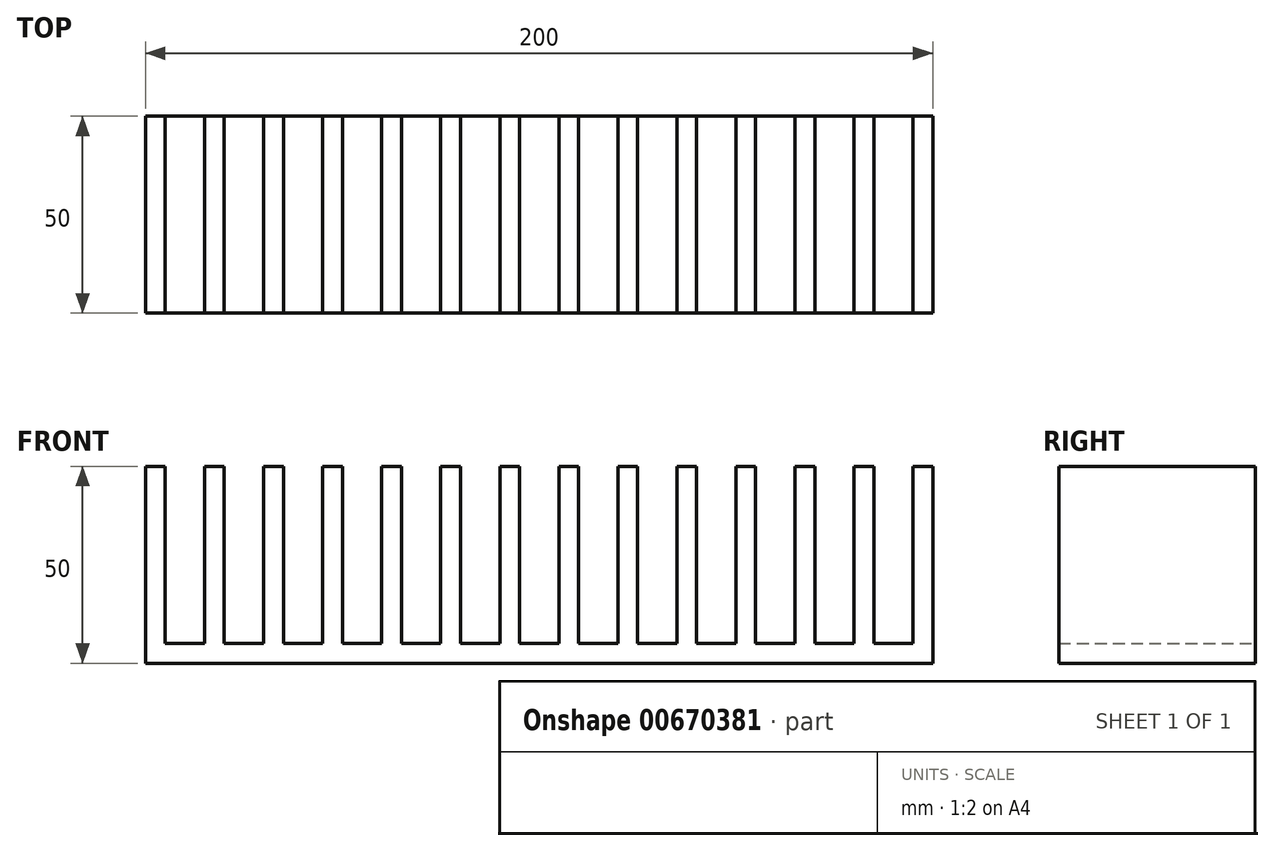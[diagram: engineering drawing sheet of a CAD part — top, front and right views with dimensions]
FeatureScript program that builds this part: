
annotation { "Feature Type Name" : "Feature", "Feature Type Description" : "" }
export const myFeature = defineFeature(function(context is Context, id is Id, definition is map)
    precondition{}
    {
        {
            var Q0;
            Q0=qCreatedBy(makeId("Top.planeOp"),FACE);
            var sketch = newSketch(context, id + "F0", { "sketchPlane" : qUnion([Q0])});
            skLineSegment(sketch, "E0.bottom", {"start": v(-104.93, 24.44) * mm, "end": v(95.07, 24.44) * mm});
            skLineSegment(sketch, "E0.top", {"start": v(-104.93, -25.56) * mm, "end": v(95.07, -25.56) * mm});
            skLineSegment(sketch, "E0.left", {"start": v(-104.93, 24.44) * mm, "end": v(-104.93, -25.56) * mm});
            skLineSegment(sketch, "E0.right", {"start": v(95.07, 24.44) * mm, "end": v(95.07, -25.56) * mm});
            skLineSegment(sketch, "E1", {"start": v(-99.93, 24.44) * mm, "end": v(-99.93, -25.56) * mm});
            skLineSegment(sketch, "E2", {"start": v(-89.93, -25.56) * mm, "end": v(-89.93, 24.44) * mm});
            skLineSegment(sketch, "E3", {"start": v(-84.93, 24.44) * mm, "end": v(-84.93, -25.56) * mm});
            skLineSegment(sketch, "E4", {"start": v(-74.93, -25.56) * mm, "end": v(-74.93, 24.44) * mm});
            skLineSegment(sketch, "E5", {"start": v(-69.93, 24.44) * mm, "end": v(-69.93, -25.56) * mm});
            skLineSegment(sketch, "E6", {"start": v(-59.93, -25.56) * mm, "end": v(-59.93, 24.44) * mm});
            skLineSegment(sketch, "E7", {"start": v(-54.93, 24.44) * mm, "end": v(-54.93, -25.56) * mm});
            skLineSegment(sketch, "E8", {"start": v(-44.93, -25.56) * mm, "end": v(-44.93, 24.44) * mm});
            skLineSegment(sketch, "E9", {"start": v(-39.93, 24.44) * mm, "end": v(-39.93, -25.56) * mm});
            skLineSegment(sketch, "E10", {"start": v(-29.93, -25.56) * mm, "end": v(-29.93, 24.44) * mm});
            skLineSegment(sketch, "E11", {"start": v(-24.93, 24.44) * mm, "end": v(-24.93, -25.56) * mm});
            skLineSegment(sketch, "E12", {"start": v(-14.93, 24.44) * mm, "end": v(-14.93, -25.56) * mm});
            skLineSegment(sketch, "E13", {"start": v(-9.93, -25.56) * mm, "end": v(-9.93, 24.44) * mm});
            skPoint(sketch, "E13.endSnap0", {"position": v(-4.93, 24.44) * mm});
            skLineSegment(sketch, "E14", {"start": v(5.07, 24.44) * mm, "end": v(5.07, -25.56) * mm});
            skLineSegment(sketch, "E15", {"start": v(0.07, -25.56) * mm, "end": v(0.07, 24.44) * mm});
            skLineSegment(sketch, "E16", {"start": v(15.07, 24.44) * mm, "end": v(15.07, -25.56) * mm});
            skLineSegment(sketch, "E17", {"start": v(20.07, -25.56) * mm, "end": v(20.07, 24.44) * mm});
            skLineSegment(sketch, "E18", {"start": v(35.07, 24.44) * mm, "end": v(35.07, -25.56) * mm});
            skLineSegment(sketch, "E19", {"start": v(30.07, -25.56) * mm, "end": v(30.07, 24.44) * mm});
            skLineSegment(sketch, "E20", {"start": v(45.07, -25.56) * mm, "end": v(45.07, 24.44) * mm});
            skLineSegment(sketch, "E21", {"start": v(50.07, 24.44) * mm, "end": v(50.07, -25.56) * mm});
            skLineSegment(sketch, "E22", {"start": v(60.07, 24.44) * mm, "end": v(60.07, -25.56) * mm});
            skLineSegment(sketch, "E23", {"start": v(65.07, -25.56) * mm, "end": v(65.07, 24.44) * mm});
            skLineSegment(sketch, "E24", {"start": v(75.07, 24.44) * mm, "end": v(75.07, -25.56) * mm});
            skLineSegment(sketch, "E25", {"start": v(80.07, -25.56) * mm, "end": v(80.07, 24.44) * mm});
            skLineSegment(sketch, "E26", {"start": v(90.07, 24.44) * mm, "end": v(90.07, -25.56) * mm});
            skSolve(sketch);
        }
        {
            var Q0;
            {var subQ0=sQuery(id+"F0.wireOp",EDGE,"E22");Q0=makeQuery(id+"F0.imprint","IMPRINT",FACE,{"disambiguationData":[TD([[makeQuery(id+"F0.imprint","IMPRINT",EDGE,{"derivedFrom":subQ0}),1.0]])]});}
            var Q1;
            {var subQ0=sQuery(id+"F0.wireOp",EDGE,"E18");Q1=makeQuery(id+"F0.imprint","IMPRINT",FACE,{"disambiguationData":[TD([[makeQuery(id+"F0.imprint","IMPRINT",EDGE,{"derivedFrom":subQ0}),1.0]])]});}
            var Q2;
            {var subQ0=sQuery(id+"F0.wireOp",EDGE,"E18");Q2=makeQuery(id+"F0.imprint","IMPRINT",FACE,{"disambiguationData":[TD([[makeQuery(id+"F0.imprint","IMPRINT",EDGE,{"derivedFrom":subQ0}),-1.0]])]});}
            var Q3;
            {var subQ0=sQuery(id+"F0.wireOp",EDGE,"E6");Q3=makeQuery(id+"F0.imprint","IMPRINT",FACE,{"disambiguationData":[TD([[makeQuery(id+"F0.imprint","IMPRINT",EDGE,{"derivedFrom":subQ0}),-1.0]])]});}
            var Q4;
            {var subQ0=sQuery(id+"F0.wireOp",EDGE,"E14");Q4=makeQuery(id+"F0.imprint","IMPRINT",FACE,{"disambiguationData":[TD([[makeQuery(id+"F0.imprint","IMPRINT",EDGE,{"derivedFrom":subQ0}),-1.0]])]});}
            var Q5;
            {var subQ0=sQuery(id+"F0.wireOp",EDGE,"E1");Q5=makeQuery(id+"F0.imprint","IMPRINT",FACE,{"disambiguationData":[TD([[makeQuery(id+"F0.imprint","IMPRINT",EDGE,{"derivedFrom":subQ0}),1.0]])]});}
            var Q6;
            {var subQ0=sQuery(id+"F0.wireOp",EDGE,"E25");Q6=makeQuery(id+"F0.imprint","IMPRINT",FACE,{"disambiguationData":[TD([[makeQuery(id+"F0.imprint","IMPRINT",EDGE,{"derivedFrom":subQ0}),-1.0]])]});}
            var Q7;
            {var subQ0=sQuery(id+"F0.wireOp",EDGE,"E24");Q7=makeQuery(id+"F0.imprint","IMPRINT",FACE,{"disambiguationData":[TD([[makeQuery(id+"F0.imprint","IMPRINT",EDGE,{"derivedFrom":subQ0}),1.0]])]});}
            var Q8;
            {var subQ0=sQuery(id+"F0.wireOp",EDGE,"E13");Q8=makeQuery(id+"F0.imprint","IMPRINT",FACE,{"disambiguationData":[TD([[makeQuery(id+"F0.imprint","IMPRINT",EDGE,{"derivedFrom":subQ0}),-1.0]])]});}
            var Q9;
            {var subQ0=sQuery(id+"F0.wireOp",EDGE,"E9");Q9=makeQuery(id+"F0.imprint","IMPRINT",FACE,{"disambiguationData":[TD([[makeQuery(id+"F0.imprint","IMPRINT",EDGE,{"derivedFrom":subQ0}),1.0]])]});}
            var Q10;
            {var subQ0=sQuery(id+"F0.wireOp",EDGE,"E0.right");Q10=makeQuery(id+"F0.imprint","IMPRINT",FACE,{"disambiguationData":[TD([[makeQuery(id+"F0.imprint","IMPRINT",EDGE,{"derivedFrom":subQ0}),-1.0]])]});}
            var Q11;
            {var subQ0=sQuery(id+"F0.wireOp",EDGE,"E4");Q11=makeQuery(id+"F0.imprint","IMPRINT",FACE,{"disambiguationData":[TD([[makeQuery(id+"F0.imprint","IMPRINT",EDGE,{"derivedFrom":subQ0}),-1.0]])]});}
            var Q12;
            {var subQ0=sQuery(id+"F0.wireOp",EDGE,"E23");Q12=makeQuery(id+"F0.imprint","IMPRINT",FACE,{"disambiguationData":[TD([[makeQuery(id+"F0.imprint","IMPRINT",EDGE,{"derivedFrom":subQ0}),-1.0]])]});}
            var Q13;
            {var subQ0=sQuery(id+"F0.wireOp",EDGE,"E8");Q13=makeQuery(id+"F0.imprint","IMPRINT",FACE,{"disambiguationData":[TD([[makeQuery(id+"F0.imprint","IMPRINT",EDGE,{"derivedFrom":subQ0}),-1.0]])]});}
            var Q14;
            {var subQ0=sQuery(id+"F0.wireOp",EDGE,"E7");Q14=makeQuery(id+"F0.imprint","IMPRINT",FACE,{"disambiguationData":[TD([[makeQuery(id+"F0.imprint","IMPRINT",EDGE,{"derivedFrom":subQ0}),1.0]])]});}
            var Q15;
            {var subQ0=sQuery(id+"F0.wireOp",EDGE,"E17");Q15=makeQuery(id+"F0.imprint","IMPRINT",FACE,{"disambiguationData":[TD([[makeQuery(id+"F0.imprint","IMPRINT",EDGE,{"derivedFrom":subQ0}),-1.0]])]});}
            var Q16;
            {var subQ0=sQuery(id+"F0.wireOp",EDGE,"E14");Q16=makeQuery(id+"F0.imprint","IMPRINT",FACE,{"disambiguationData":[TD([[makeQuery(id+"F0.imprint","IMPRINT",EDGE,{"derivedFrom":subQ0}),1.0]])]});}
            var Q17;
            {var subQ0=sQuery(id+"F0.wireOp",EDGE,"E5");Q17=makeQuery(id+"F0.imprint","IMPRINT",FACE,{"disambiguationData":[TD([[makeQuery(id+"F0.imprint","IMPRINT",EDGE,{"derivedFrom":subQ0}),1.0]])]});}
            var Q18;
            {var subQ0=sQuery(id+"F0.wireOp",EDGE,"E20");Q18=makeQuery(id+"F0.imprint","IMPRINT",FACE,{"disambiguationData":[TD([[makeQuery(id+"F0.imprint","IMPRINT",EDGE,{"derivedFrom":subQ0}),-1.0]])]});}
            var Q19;
            {var subQ0=sQuery(id+"F0.wireOp",EDGE,"E3");Q19=makeQuery(id+"F0.imprint","IMPRINT",FACE,{"disambiguationData":[TD([[makeQuery(id+"F0.imprint","IMPRINT",EDGE,{"derivedFrom":subQ0}),1.0]])]});}
            var Q20;
            {var subQ0=sQuery(id+"F0.wireOp",EDGE,"E10");Q20=makeQuery(id+"F0.imprint","IMPRINT",FACE,{"disambiguationData":[TD([[makeQuery(id+"F0.imprint","IMPRINT",EDGE,{"derivedFrom":subQ0}),-1.0]])]});}
            var Q21;
            {var subQ0=sQuery(id+"F0.wireOp",EDGE,"E0.left");Q21=makeQuery(id+"F0.imprint","IMPRINT",FACE,{"disambiguationData":[TD([[makeQuery(id+"F0.imprint","IMPRINT",EDGE,{"derivedFrom":subQ0}),1.0]])]});}
            var Q22;
            {var subQ0=sQuery(id+"F0.wireOp",EDGE,"E12");Q22=makeQuery(id+"F0.imprint","IMPRINT",FACE,{"disambiguationData":[TD([[makeQuery(id+"F0.imprint","IMPRINT",EDGE,{"derivedFrom":subQ0}),1.0]])]});}
            var Q23;
            {var subQ0=sQuery(id+"F0.wireOp",EDGE,"E11");Q23=makeQuery(id+"F0.imprint","IMPRINT",FACE,{"disambiguationData":[TD([[makeQuery(id+"F0.imprint","IMPRINT",EDGE,{"derivedFrom":subQ0}),1.0]])]});}
            var Q24;
            {var subQ0=sQuery(id+"F0.wireOp",EDGE,"E2");Q24=makeQuery(id+"F0.imprint","IMPRINT",FACE,{"disambiguationData":[TD([[makeQuery(id+"F0.imprint","IMPRINT",EDGE,{"derivedFrom":subQ0}),-1.0]])]});}
            var Q25;
            {var subQ0=sQuery(id+"F0.wireOp",EDGE,"E21");Q25=makeQuery(id+"F0.imprint","IMPRINT",FACE,{"disambiguationData":[TD([[makeQuery(id+"F0.imprint","IMPRINT",EDGE,{"derivedFrom":subQ0}),1.0]])]});}
            var Q26;
            {var subQ0=sQuery(id+"F0.wireOp",EDGE,"E16");Q26=makeQuery(id+"F0.imprint","IMPRINT",FACE,{"disambiguationData":[TD([[makeQuery(id+"F0.imprint","IMPRINT",EDGE,{"derivedFrom":subQ0}),1.0]])]});}
            extrude(context, id + "F1", {"entities" : qUnion([Q0, Q1, Q2, Q3, Q4, Q5, Q6, Q7, Q8, Q9, Q10, Q11, Q12, Q13, Q14, Q15, Q16, Q17, Q18, Q19, Q20, Q21, Q22, Q23, Q24, Q25, Q26]), "depth" : 5 * mm, "offsetDistance" : 25 * mm});
        }
        {
            var Q0;
            {var subQ0=sQuery(id+"F0.wireOp",EDGE,"E0.left");Q0=makeQuery(id+"F0.imprint","IMPRINT",FACE,{"disambiguationData":[TD([[makeQuery(id+"F0.imprint","IMPRINT",EDGE,{"derivedFrom":subQ0}),1.0]])]});}
            var Q1;
            {var subQ0=sQuery(id+"F0.wireOp",EDGE,"E2");Q1=makeQuery(id+"F0.imprint","IMPRINT",FACE,{"disambiguationData":[TD([[makeQuery(id+"F0.imprint","IMPRINT",EDGE,{"derivedFrom":subQ0}),-1.0]])]});}
            var Q2;
            {var subQ0=sQuery(id+"F0.wireOp",EDGE,"E4");Q2=makeQuery(id+"F0.imprint","IMPRINT",FACE,{"disambiguationData":[TD([[makeQuery(id+"F0.imprint","IMPRINT",EDGE,{"derivedFrom":subQ0}),-1.0]])]});}
            var Q3;
            {var subQ0=sQuery(id+"F0.wireOp",EDGE,"E6");Q3=makeQuery(id+"F0.imprint","IMPRINT",FACE,{"disambiguationData":[TD([[makeQuery(id+"F0.imprint","IMPRINT",EDGE,{"derivedFrom":subQ0}),-1.0]])]});}
            var Q4;
            {var subQ0=sQuery(id+"F0.wireOp",EDGE,"E8");Q4=makeQuery(id+"F0.imprint","IMPRINT",FACE,{"disambiguationData":[TD([[makeQuery(id+"F0.imprint","IMPRINT",EDGE,{"derivedFrom":subQ0}),-1.0]])]});}
            var Q5;
            {var subQ0=sQuery(id+"F0.wireOp",EDGE,"E10");Q5=makeQuery(id+"F0.imprint","IMPRINT",FACE,{"disambiguationData":[TD([[makeQuery(id+"F0.imprint","IMPRINT",EDGE,{"derivedFrom":subQ0}),-1.0]])]});}
            var Q6;
            {var subQ0=sQuery(id+"F0.wireOp",EDGE,"E12");Q6=makeQuery(id+"F0.imprint","IMPRINT",FACE,{"disambiguationData":[TD([[makeQuery(id+"F0.imprint","IMPRINT",EDGE,{"derivedFrom":subQ0}),1.0]])]});}
            var Q7;
            {var subQ0=sQuery(id+"F0.wireOp",EDGE,"E14");Q7=makeQuery(id+"F0.imprint","IMPRINT",FACE,{"disambiguationData":[TD([[makeQuery(id+"F0.imprint","IMPRINT",EDGE,{"derivedFrom":subQ0}),-1.0]])]});}
            var Q8;
            {var subQ0=sQuery(id+"F0.wireOp",EDGE,"E16");Q8=makeQuery(id+"F0.imprint","IMPRINT",FACE,{"disambiguationData":[TD([[makeQuery(id+"F0.imprint","IMPRINT",EDGE,{"derivedFrom":subQ0}),1.0]])]});}
            var Q9;
            {var subQ0=sQuery(id+"F0.wireOp",EDGE,"E18");Q9=makeQuery(id+"F0.imprint","IMPRINT",FACE,{"disambiguationData":[TD([[makeQuery(id+"F0.imprint","IMPRINT",EDGE,{"derivedFrom":subQ0}),-1.0]])]});}
            var Q10;
            {var subQ0=sQuery(id+"F0.wireOp",EDGE,"E20");Q10=makeQuery(id+"F0.imprint","IMPRINT",FACE,{"disambiguationData":[TD([[makeQuery(id+"F0.imprint","IMPRINT",EDGE,{"derivedFrom":subQ0}),-1.0]])]});}
            var Q11;
            {var subQ0=sQuery(id+"F0.wireOp",EDGE,"E22");Q11=makeQuery(id+"F0.imprint","IMPRINT",FACE,{"disambiguationData":[TD([[makeQuery(id+"F0.imprint","IMPRINT",EDGE,{"derivedFrom":subQ0}),1.0]])]});}
            var Q12;
            {var subQ0=sQuery(id+"F0.wireOp",EDGE,"E24");Q12=makeQuery(id+"F0.imprint","IMPRINT",FACE,{"disambiguationData":[TD([[makeQuery(id+"F0.imprint","IMPRINT",EDGE,{"derivedFrom":subQ0}),1.0]])]});}
            var Q13;
            {var subQ0=sQuery(id+"F0.wireOp",EDGE,"E0.right");Q13=makeQuery(id+"F0.imprint","IMPRINT",FACE,{"disambiguationData":[TD([[makeQuery(id+"F0.imprint","IMPRINT",EDGE,{"derivedFrom":subQ0}),-1.0]])]});}
            extrude(context, id + "F2", {"entities" : qUnion([Q0, Q1, Q2, Q3, Q4, Q5, Q6, Q7, Q8, Q9, Q10, Q11, Q12, Q13]), "operationType" : NewBodyOperationType.ADD, "depth" : 50 * mm, "offsetDistance" : 25 * mm});
        }
    });
